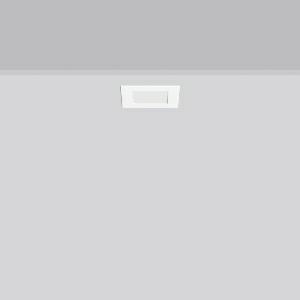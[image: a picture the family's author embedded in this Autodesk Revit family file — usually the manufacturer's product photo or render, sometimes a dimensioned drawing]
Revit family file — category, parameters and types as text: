
# Revit family: toledo_flat_square_e_672241_002_d60f
name_source: partatom
category: Lighting Fixtures
units: mm (PartAtom-declared; Revit-internal decimal feet)

## family parameters
Cut with Voids When Loaded = No
Host = Face
Light Source = No
Part Type = Normal
Room Calculation Point = No
Round Connector Dimension = Use Diameter
Shared = No

## types (1)
- TOLEDO FLAT square E (1 x LED Modul 830, 370 lm, 3000)
    Apparent Load = 5 VA
    CIE Flux Codes = 49 80 96 100 100
    Color Rendering = 80
    Color Temperature = 3000
    Default Elevation = 1800 mm
    Description = Series: TOLEDO FLAT square
Square recessed downlight. For escape route illumination. Housing: die-cast aluminium, powder-coated. Lightguide and diffuser made of non-yellowing plastic (PMMA). Diffuser opal matt plastic. Ceiling installation with spring system. Including separate LED converter with connecting cable 250 mm. Suitable for connection to central battery systems. External driver with simple plug-in locking system. 
Colour: white
Length: 110 mm
Width: 110 mm
Height: 3 mm
Cut-out length: 96 mm
Cut-out width: 96 mm
Recess height: 40 mm
Luminaire: recess height: 31-51 mm
Weight: 243 g
Operating mode: maintained power mode
Lamp: LED
Socket: without socket
Colour temperature: 3000K
Colour rendering index (CRI): 80
System power: 4.7 W
Rated luminous flux: 370 lm
Luminous flux, emergency: 370 lm
System power, emergency: 4.7 W
Control gear: Regulated power supply
Protection class: II
Type of protection: IP 54
    Height = 0 mm  [stored 0 ft]
    Lamp = 1 x LED Modul 830
    Lamp Light Flux = 370 lm
    Lamp count = 1
    Length = 110 mm
    Lifetime = 50000 h
    Luminous efficacy = 79 lm/W
    Manufacturer = RZB
    ModVariant = No
    Model = 672241.002
    Mounting Place = Ceiling
    Mounting Type = Recessed
    Number of Poles = 1
    OnlyDefault = Yes
    Power Factor = 1
    Product Name = TOLEDO FLAT square E
    Product group = Recessed downlights
    ProductGroupID = 402
    Protection Class = Protection class II
    Protection Degree = IP 40
    RLX_Detail_Level = 1
    RLX_Emergency_Light_Flux = 370 lm
    RLX_Emergency_Type = 3
    RLX_Emergency_Type_DB = Yes
    RlxData = <blob elided: 9613 chars, md5=32ca3e98>
    Socket = socket
    Standby Power = 0 W
    System Light Flux = 370 lm
    System Power = 5 W
    Type Comments = Product without accessories
    Type Image = 901485.002.jpg
    URL = http://relux.com
    VarID = ---
    Voltage = 230 V
    Voltage Range = 220-240 V
    Weight = 0.00 kg
    Width = 110 mm

note: [stored X ft] marks values corroborated as IEEE doubles in the binary element streams (Revit-internal decimal feet)

## geometry (parser evidence)
native form markers: Sweep x9
no freeform markers — native parametric forms only
